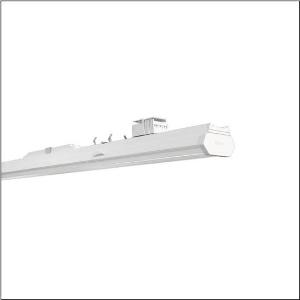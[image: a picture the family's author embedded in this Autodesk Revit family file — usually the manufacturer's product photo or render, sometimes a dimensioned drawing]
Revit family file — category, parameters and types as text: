
# Revit family: licross_r__21_protected_mo_52td12dnd75f_7536
name_source: partatom
category: Lighting Fixtures
units: mm (PartAtom-declared; Revit-internal decimal feet)

## family parameters
Cut with Voids When Loaded = No
Host = Face
Light Source = No
Part Type = Normal
Room Calculation Point = No
Round Connector Dimension = Use Diameter
Shared = No

## types (1)
- --- (1 x LED, 7710 lm, 61 W, 4000K)
    Apparent Load = 61 VA
    CIE Flux Codes = 73 92 98 99 100
    Color Rendering = 90
    Color Temperature = 4000K
    Default Elevation = 1800 mm
    Description = Licross® 21 Protected MO, luminaire insert, of sheet steel, galvanised, coil coated, white, length: 1.500mm, width: 90mm, height: 101mm, LED rated luminous flux: 7.710lm, light colour: 940, control gear: DALI 2, control gear: ECG DALI, with plug, 5-pole, with phase selection, mains connection: 220..240V, AC, 50/60Hz, rated input power: 61W, halogen-free wiring, primary optical cover: cover, of PMMA, light emission: direct distribution, primary light characteristic: symmetric, protection rating (complete): IP54, insulation class (complete): insulation class I (protective earthing), certification: CE, ENEC, VDE, UKCA, protection symbol: D if used in an environment with non-conductive dust loads with corresponding accessories, impact resistance: IK06, permissible ambient temperature for indoor applications: -25..+40°C, corresponds to IFS (International Featured Standards) requirements for safety and quality in the food industry, reducing of maximum allowable ambient temperature of 5°C with ceiling mounting, LABS conformity tested according to VDMA 24364:2018-05, packaging unit: 1 piece
    Height = 92 mm
    Lamp = 1 x LED
    Lamp Light Flux = 7710 lm
    Lamp Power = 61 W
    Lamp count = 1
    Length = 1500 mm
    Luminous efficacy = 126 lm/W
    Manufacturer = Siteco
    ModVariant = No
    Model = 52TD12DND75F
    Mounting Place = Ceiling
    Mounting Type = Pendant
    Number of Poles = 1
    OnlyDefault = Yes
    Power Factor = 1
    Product Name = Licross® 21 Protected MO
    Product group = luminaire insert
    ProductGroupID = 901
    Protection Class = Protection class I
    Protection Degree = IP 54
    RLX_Detail_Level = 1
    RLX_Emergency_Light_Flux = 0 lm
    RLX_Emergency_Type = 0
    RLX_Emergency_Type_DB = No
    RlxData = <blob elided: 24325 chars, md5=a14dabbd>
    Socket = socket
    Standby Power = 0 W
    System Light Flux = 7710 lm
    System Power = 61 W
    Type Comments = factory setting: luminous flux: 100 % | dim-lin: 254 | 405 mA
    Type Image = l_1256148.jpg
    URL = http://relux.com
    VarID = @adj_136401
    Voltage = 0 V
    Weight = 0.00 kg
    Width = 88 mm

## geometry (parser evidence)
native form markers: Blend x4, Sweep x11
no freeform markers — native parametric forms only
